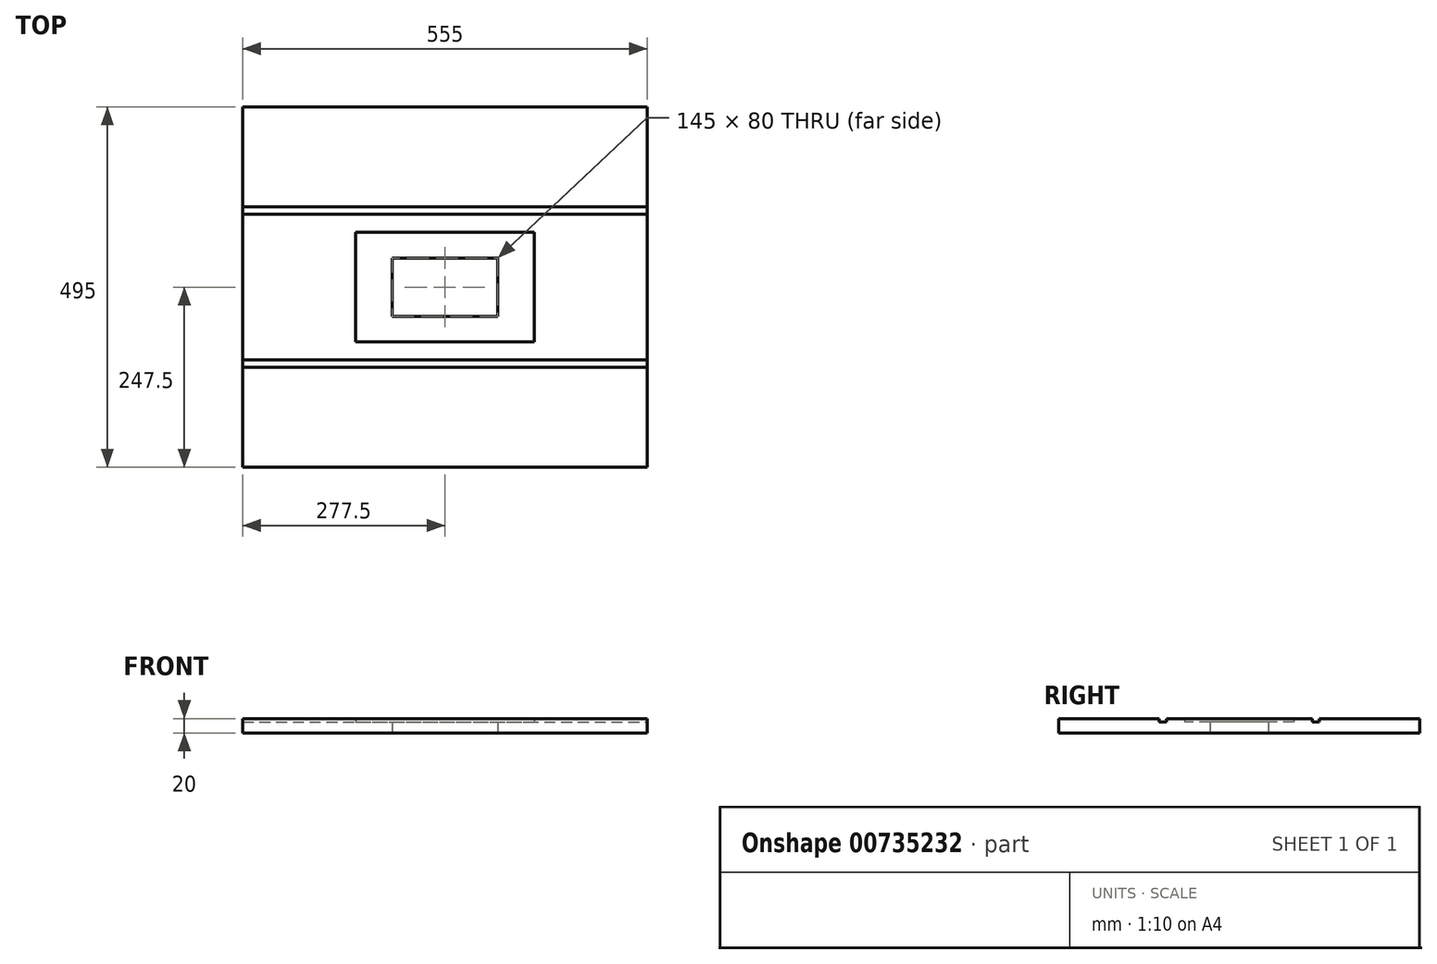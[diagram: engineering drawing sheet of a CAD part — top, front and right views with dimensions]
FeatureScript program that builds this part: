
annotation { "Feature Type Name" : "Feature", "Feature Type Description" : "" }
export const myFeature = defineFeature(function(context is Context, id is Id, definition is map)
    precondition{}
    {
        {
            var Q0;
            Q0=qCreatedBy(makeId("Top.planeOp"),FACE);
            var sketch = newSketch(context, id + "F0", { "sketchPlane" : qUnion([Q0])});
            skLineSegment(sketch, "E0.bottom", {"start": v(0, 0) * mm, "end": v(555, 0) * mm});
            skLineSegment(sketch, "E0.top", {"start": v(0, 495) * mm, "end": v(555, 495) * mm});
            skLineSegment(sketch, "E0.left", {"start": v(0, 0) * mm, "end": v(0, 495) * mm});
            skLineSegment(sketch, "E0.right", {"start": v(555, 0) * mm, "end": v(555, 495) * mm});
            skLineSegment(sketch, "E1.bottom", {"start": v(155, 322.5) * mm, "end": v(400, 322.5) * mm});
            skLineSegment(sketch, "E1.top", {"start": v(155, 172.5) * mm, "end": v(400, 172.5) * mm});
            skLineSegment(sketch, "E1.left", {"start": v(155, 322.5) * mm, "end": v(155, 172.5) * mm});
            skLineSegment(sketch, "E1.right", {"start": v(400, 322.5) * mm, "end": v(400, 172.5) * mm});
            skLineSegment(sketch, "E2.bottom", {"start": v(205, 287.5) * mm, "end": v(350, 287.5) * mm});
            skLineSegment(sketch, "E2.top", {"start": v(205, 207.5) * mm, "end": v(350, 207.5) * mm});
            skLineSegment(sketch, "E2.left", {"start": v(205, 287.5) * mm, "end": v(205, 207.5) * mm});
            skLineSegment(sketch, "E2.right", {"start": v(350, 287.5) * mm, "end": v(350, 207.5) * mm});
            skLineSegment(sketch, "E3.bottom", {"start": v(0, 147.5) * mm, "end": v(555, 147.5) * mm});
            skLineSegment(sketch, "E3.top", {"start": v(0, 137.5) * mm, "end": v(555, 137.5) * mm});
            skLineSegment(sketch, "E3.left", {"start": v(0, 147.5) * mm, "end": v(0, 137.5) * mm});
            skLineSegment(sketch, "E3.right", {"start": v(555, 147.5) * mm, "end": v(555, 137.5) * mm});
            skLineSegment(sketch, "E4.bottom", {"start": v(0, 357.5) * mm, "end": v(555, 357.5) * mm});
            skLineSegment(sketch, "E4.top", {"start": v(0, 347.5) * mm, "end": v(555, 347.5) * mm});
            skLineSegment(sketch, "E4.left", {"start": v(0, 357.5) * mm, "end": v(0, 347.5) * mm});
            skLineSegment(sketch, "E4.right", {"start": v(555, 357.5) * mm, "end": v(555, 347.5) * mm});
            skSolve(sketch);
        }
        {
            var Q0;
            Q0=makeQuery(id+"F0.imprint","IMPRINT",FACE,{"disambiguationData":[TD([[makeQuery(id+"F0.imprint","IMPRINT",EDGE,{"derivedFrom":sQuery(id+"F0.wireOp",EDGE,"E0.bottom")}),1.0]])]});
            var Q1;
            {var subQ0=sQuery(id+"F0.wireOp",EDGE,"E0.top");Q1=makeQuery(id+"F0.imprint","IMPRINT",FACE,{"disambiguationData":[TD([[makeQuery(id+"F0.imprint","IMPRINT",EDGE,{"derivedFrom":subQ0}),-1.0]])]});}
            var Q2;
            Q2=makeQuery(id+"F0.imprint","IMPRINT",FACE,{"disambiguationData":[TD([[makeQuery(id+"F0.imprint","IMPRINT",EDGE,{"derivedFrom":sQuery(id+"F0.wireOp",EDGE,"E1.bottom")}),1.0]])]});
            extrude(context, id + "F1", {"entities" : qUnion([Q0, Q1, Q2]), "depth" : 20 * mm, "offsetDistance" : 25 * mm});
        }
        {
            var Q0;
            Q0=makeQuery(id+"F0.imprint","IMPRINT",FACE,{"disambiguationData":[TD([[makeQuery(id+"F0.imprint","IMPRINT",EDGE,{"derivedFrom":sQuery(id+"F0.wireOp",EDGE,"E1.bottom")}),-1.0]])]});
            var Q1;
            Q1=makeQuery(id+"F0.imprint","IMPRINT",FACE,{"disambiguationData":[TD([[makeQuery(id+"F0.imprint","IMPRINT",EDGE,{"derivedFrom":sQuery(id+"F0.wireOp",EDGE,"E4.bottom")}),-1.0]])]});
            var Q2;
            Q2=makeQuery(id+"F0.imprint","IMPRINT",FACE,{"disambiguationData":[TD([[makeQuery(id+"F0.imprint","IMPRINT",EDGE,{"derivedFrom":sQuery(id+"F0.wireOp",EDGE,"E3.bottom")}),-1.0]])]});
            extrude(context, id + "F2", {"entities" : qUnion([Q0, Q1, Q2]), "operationType" : NewBodyOperationType.ADD, "depth" : 15 * mm, "offsetDistance" : 25 * mm});
        }
    });
